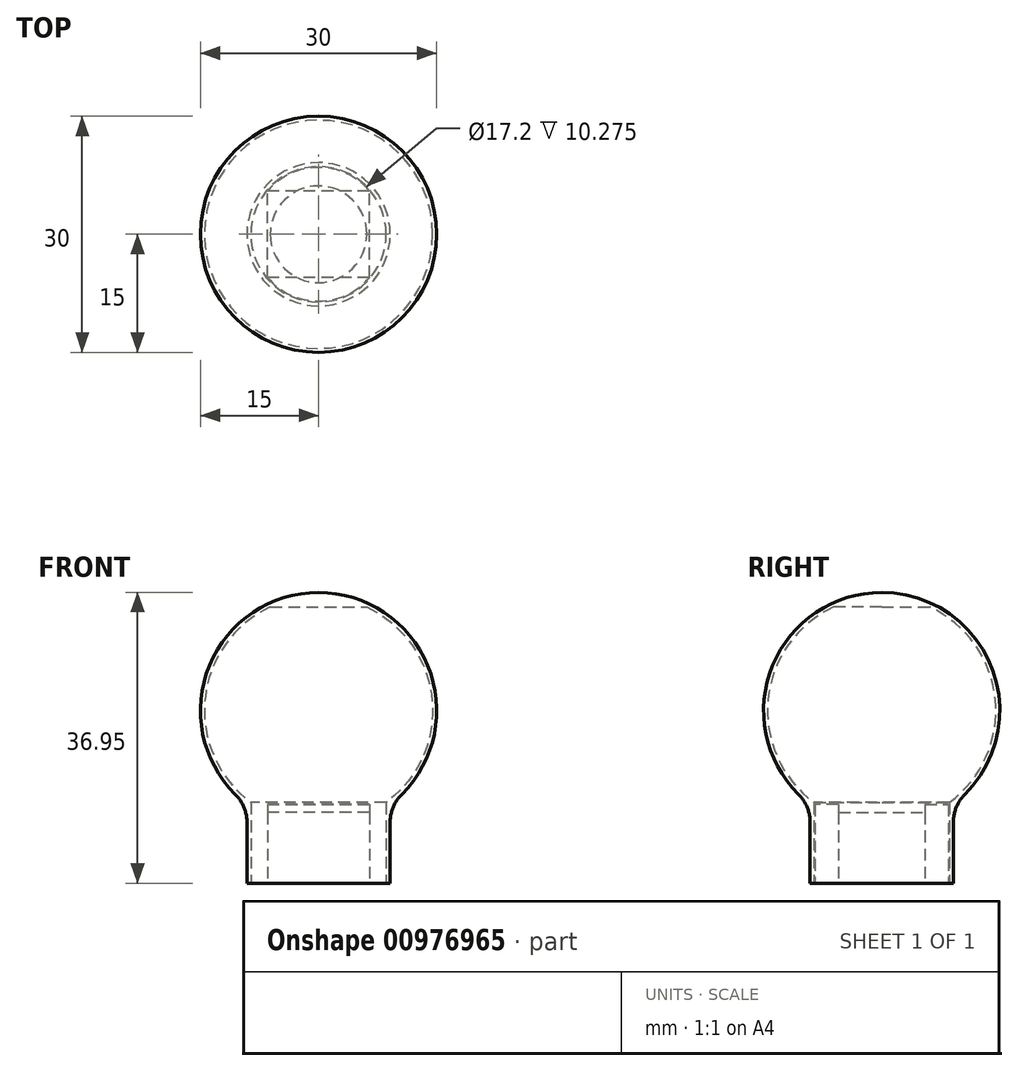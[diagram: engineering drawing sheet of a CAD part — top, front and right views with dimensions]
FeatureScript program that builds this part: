
annotation { "Feature Type Name" : "Feature", "Feature Type Description" : "" }
export const myFeature = defineFeature(function(context is Context, id is Id, definition is map)
    precondition{}
    {
        {
            var Q0;
            Q0=qCreatedBy(makeId("Top.planeOp"),FACE);
            var sketch = newSketch(context, id + "F0", { "sketchPlane" : qUnion([Q0])});
            skCircle(sketch, "E0", {"center": v(0, 0) * mm, "radius": 9.1 * mm});
            skCircle(sketch, "E1", {"center": v(0, 0) * mm, "radius": 8.6 * mm});
            skSolve(sketch);
        }
        {
            var Q0;
            Q0 = qSketchRegion(id + "F0", true);
            extrude(context, id + "F1", {"entities" : qUnion([Q0]), "depth" : 10 * mm, "offsetDistance" : 25 * mm});
        }
        {
            var Q0;
            Q0=qCreatedBy(makeId("Right.planeOp"),FACE);
            var sketch = newSketch(context, id + "F2", { "sketchPlane" : qUnion([Q0])});
            skArc(sketch, "E2", {"start": v(5.36, 7.94) * mm, "mid": v(14.75, 24.68) * mm, "end": v(0, 36.95) * mm});
            skLineSegment(sketch, "E3", {"start": v(5.36, 7.94) * mm, "end": v(0, 7.94) * mm});
            skLineSegment(sketch, "E4", {"start": v(0, -11.4) * mm, "end": v(0, 41.78) * mm, "construction": true});
            skLineSegment(sketch, "E5.0", {"start": v(5.27, 8.44) * mm, "end": v(0, 8.44) * mm});
            skArc(sketch, "E5.1", {"start": v(5.27, 8.44) * mm, "mid": v(14.25, 24.63) * mm, "end": v(0, 36.45) * mm});
            skLineSegment(sketch, "E6", {"start": v(0, 36.95) * mm, "end": v(0, 7.94) * mm});
            skLineSegment(sketch, "E7", {"start": v(6.13, 35.09) * mm, "end": v(0, 35.09) * mm});
            skPoint(sketch, "E8", {"position": v(0, 15.19) * mm});
            skSolve(sketch);
        }
        {
            var Q0;
            {var subQ3=sQuery(id+"F2.wireOp",EDGE,"E2");Q0=makeQuery(id+"F2.imprint","IMPRINT",FACE,{"disambiguationData":[TD([[makeQuery(id+"F2.imprint","IMPRINT",EDGE,{"derivedFrom":subQ3}),1.0]])]});}
            var Q1;
            {var subQ3=sQuery(id+"F2.wireOp",EDGE,"E7");Q1=makeQuery(id+"F2.imprint","IMPRINT",FACE,{"disambiguationData":[TD([[makeQuery(id+"F2.imprint","IMPRINT",EDGE,{"derivedFrom":subQ3}),-1.0]])]});}
            var Q2;
            Q2=sQuery(id+"F2.wireOp",EDGE,"E4");
            revolve(context, id + "F3", {"operationType" : NewBodyOperationType.ADD, "surfaceOperationType" : NewSurfaceOperationType.NEW, "entities" : qUnion([Q0, Q1]), "axis" : qUnion([Q2]), "revolveType" : RevolveType.FULL});
        }
        {
            var Q0;
            Q0=makeQuery(id+"F0.imprint","IMPRINT",FACE,{"disambiguationData":[TD([[makeQuery(id+"F0.imprint","IMPRINT",EDGE,{"derivedFrom":sQuery(id+"F0.wireOp",EDGE,"E1")}),1.0]])]});
            extrude(context, id + "F4", {"entities" : qUnion([Q0]), "operationType" : NewBodyOperationType.REMOVE, "depth" : 15 * mm, "offsetDistance" : 25 * mm});
        }
        {
            var Q0;
            Q0=qCreatedBy(makeId("Top.planeOp"),FACE);
            var sketch = newSketch(context, id + "F5", { "sketchPlane" : qUnion([Q0])});
            skArc(sketch, "E9", {"start": v(6.48, 5.5) * mm, "mid": v(0, 8.5) * mm, "end": v(-6.48, 5.5) * mm});
            skLineSegment(sketch, "E10.bottom", {"start": v(-6.48, -5.5) * mm, "end": v(6.48, -5.5) * mm});
            skLineSegment(sketch, "E10.top", {"start": v(-6.48, 5.5) * mm, "end": v(6.48, 5.5) * mm});
            skLineSegment(sketch, "E10.left", {"start": v(-6.48, -5.5) * mm, "end": v(-6.48, 5.5) * mm});
            skLineSegment(sketch, "E10.right", {"start": v(6.48, -5.5) * mm, "end": v(6.48, 5.5) * mm});
            skArc(sketch, "E11.trimOffspring", {"start": v(-6.48, -5.5) * mm, "mid": v(0, -8.5) * mm, "end": v(6.48, -5.5) * mm});
            skSolve(sketch);
        }
        {
            var Q0;
            Q0 = qSketchRegion(id + "F5", true);
            extrude(context, id + "F6", {"entities" : qUnion([Q0]), "depth" : 10 * mm, "offsetDistance" : 25 * mm});
        }
        {
            var Q0;
            Q0=makeQuery(id+"F6.opExtrude","CAP_FACE",FACE,{"disambiguationData":[OSD([sQuery(id+"F5.wireOp",EDGE,"E9"),sQuery(id+"F5.wireOp",EDGE,"E10.left"),sQuery(id+"F5.wireOp",EDGE,"E10.right"),sQuery(id+"F5.wireOp",EDGE,"E11.trimOffspring")])],"isStart":false});
            var sketch = newSketch(context, id + "F7", { "sketchPlane" : qUnion([Q0])});
            skLineSegment(sketch, "E12", {"start": v(6.48, 5.5) * mm, "end": v(-6.48, 5.5) * mm});
            skLineSegment(sketch, "E13", {"start": v(6.48, -5.5) * mm, "end": v(-6.48, -5.5) * mm});
            skSolve(sketch);
        }
        {
            var Q0;
            Q0=makeQuery(id+"F7.imprint","IMPRINT",FACE,{"disambiguationData":[TD([[makeQuery(id+"F7.imprint","IMPRINT",EDGE,{"derivedFrom":sQuery(id+"F7.wireOp",EDGE,"E12")}),1.0]])]});
            extrude(context, id + "F8", {"entities" : qUnion([Q0]), "operationType" : NewBodyOperationType.REMOVE, "oppositeDirection" : true, "depth" : 1 * mm, "offsetDistance" : 25 * mm});
        }
        {
            var Q0;
            Q0=makeQuery(id+"F1.opExtrude","CAP_EDGE",EDGE,{"disambiguationData":[OSD([sQuery(id+"F0.wireOp",EDGE,"E0")])],"isStart":false});
            fillet(context, id + "F9", {"entities" : qUnion([Q0]), "radius" : 5 * mm, "tangentPropagation" : true, "allowEdgeOverflow" : false});
        }
        {
            var Q0;
            Q0=makeQuery(id+"F3.boolean.opBoolean","SPLIT",FACE,{"disambiguationData":[TD([makeQuery(id+"F1.opExtrude","CAP_FACE",FACE,{"disambiguationData":[OSD([sQuery(id+"F0.wireOp",EDGE,"E0"),sQuery(id+"F0.wireOp",EDGE,"E1")])],"isStart":false})])],"derivedFrom":makeQuery(id+"F3.opRevolve","SWEPT_FACE",FACE,{"disambiguationData":[OSD([sQuery(id+"F2.wireOp",EDGE,"E2")])]})});
            fillet(context, id + "F10", {"entities" : qUnion([Q0]), "tangentPropagation" : true, "radius" : 5 * mm, "defaultsChanged" : false, "vertexSettings" : [], "allowEdgeOverflow" : false});
        }
    });
